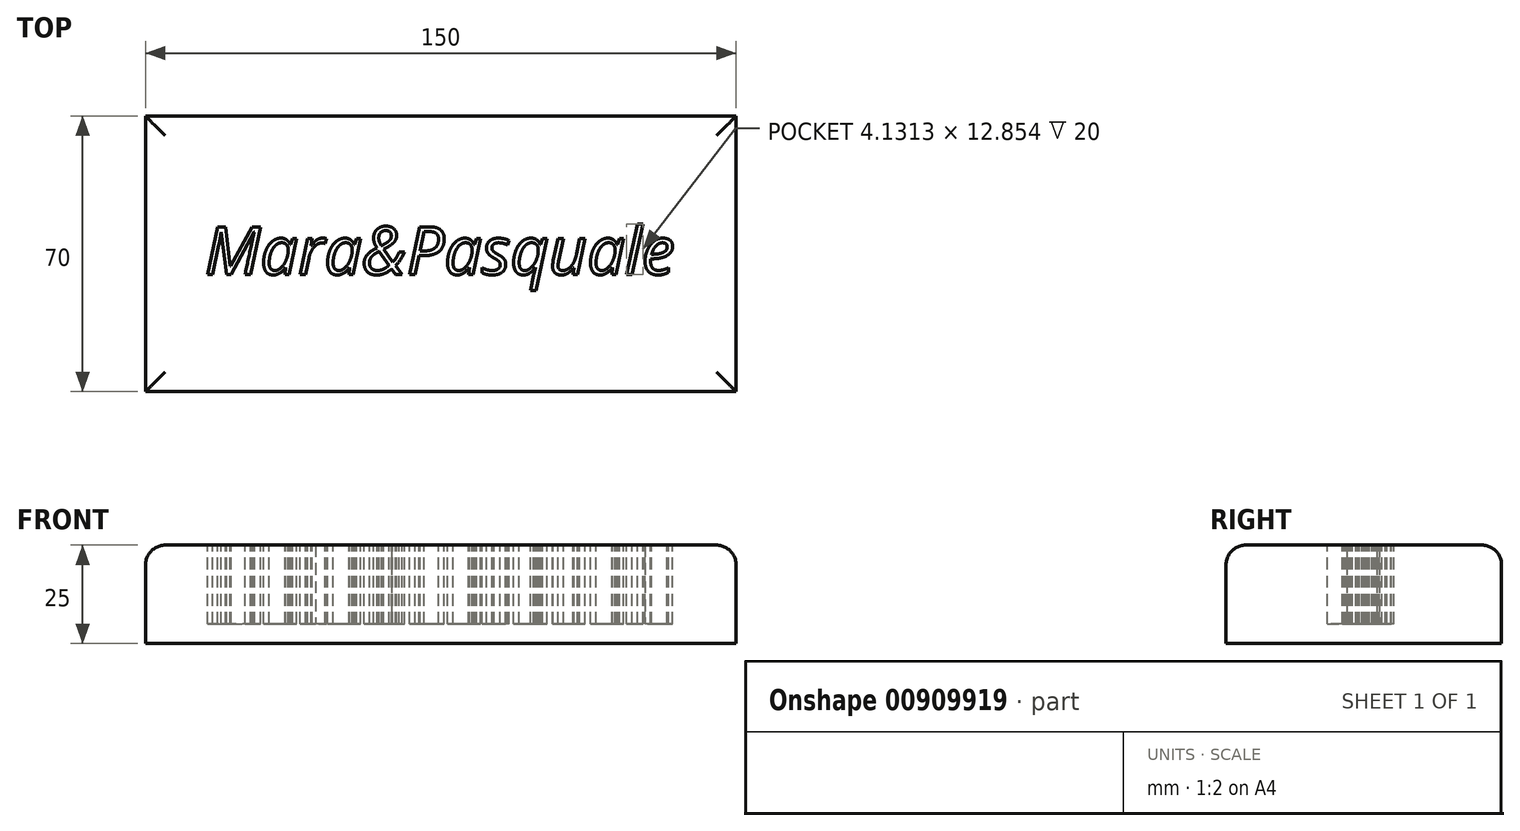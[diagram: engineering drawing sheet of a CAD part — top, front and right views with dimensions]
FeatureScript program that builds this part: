
annotation { "Feature Type Name" : "Feature", "Feature Type Description" : "" }
export const myFeature = defineFeature(function(context is Context, id is Id, definition is map)
    precondition{}
    {
        {
            var Q0;
            Q0=qCreatedBy(makeId("Top.planeOp"),FACE);
            var sketch = newSketch(context, id + "F0", { "sketchPlane" : qUnion([Q0])});
            skLineSegment(sketch, "E0.bottom", {"start": v(-75, 35) * mm, "end": v(75, 35) * mm});
            skLineSegment(sketch, "E0.top", {"start": v(-75, -35) * mm, "end": v(75, -35) * mm});
            skLineSegment(sketch, "E0.left", {"start": v(-75, 35) * mm, "end": v(-75, -35) * mm});
            skLineSegment(sketch, "E0.right", {"start": v(75, 35) * mm, "end": v(75, -35) * mm});
            skPoint(sketch, "E0.middle", {"position": v(0, 0) * mm});
            skSolve(sketch);
        }
        {
            var Q0;
            Q0=makeQuery(id+"F0.imprint","IMPRINT",FACE,{"disambiguationData":[TD([[makeQuery(id+"F0.imprint","IMPRINT",EDGE,{"derivedFrom":sQuery(id+"F0.wireOp",EDGE,"E0.bottom")}),-1.0]])]});
            extrude(context, id + "F1", {"entities" : qUnion([Q0]), "depth" : 25 * mm, "offsetDistance" : 25 * mm});
        }
        {
            var Q0;
            Q0=makeQuery(id+"F1.opExtrude","CAP_FACE",FACE,{"disambiguationData":[OSD([sQuery(id+"F0.wireOp",EDGE,"E0.bottom"),sQuery(id+"F0.wireOp",EDGE,"E0.top"),sQuery(id+"F0.wireOp",EDGE,"E0.left"),sQuery(id+"F0.wireOp",EDGE,"E0.right")])],"isStart":false});
            var sketch = newSketch(context, id + "F2", { "sketchPlane" : qUnion([Q0])});
            skText(sketch, "E1", { "text": "Mara&Pasquale", "fontName": "OpenSans-Italic.ttf"});
            const initialGuessF2  = {"E1": [-0.06, -0.00523, 1, 0, 0.01218]};
            skSetInitialGuess(sketch, initialGuessF2);
            skSolve(sketch);
        }
        {
            var Q0;
            Q0 = qSketchRegion(id + "F2", true);
            extrude(context, id + "F3", {"entities" : qUnion([Q0]), "operationType" : NewBodyOperationType.REMOVE, "oppositeDirection" : true, "depth" : 20 * mm, "offsetDistance" : 25 * mm});
        }
        {
            var Q0;
            Q0=makeQuery(id+"F1.opExtrude","CAP_EDGE",EDGE,{"disambiguationData":[OSD([sQuery(id+"F0.wireOp",EDGE,"E0.left")])],"isStart":false});
            var Q1;
            Q1=makeQuery(id+"F1.opExtrude","CAP_EDGE",EDGE,{"disambiguationData":[OSD([sQuery(id+"F0.wireOp",EDGE,"E0.bottom")])],"isStart":false});
            var Q2;
            Q2=makeQuery(id+"F1.opExtrude","CAP_EDGE",EDGE,{"disambiguationData":[OSD([sQuery(id+"F0.wireOp",EDGE,"E0.right")])],"isStart":false});
            var Q3;
            Q3=makeQuery(id+"F1.opExtrude","CAP_EDGE",EDGE,{"disambiguationData":[OSD([sQuery(id+"F0.wireOp",EDGE,"E0.top")])],"isStart":false});
            fillet(context, id + "F4", {"entities" : qUnion([Q0, Q1, Q2, Q3]), "radius" : 5 * mm, "tangentPropagation" : true, "allowEdgeOverflow" : false});
        }
    });
